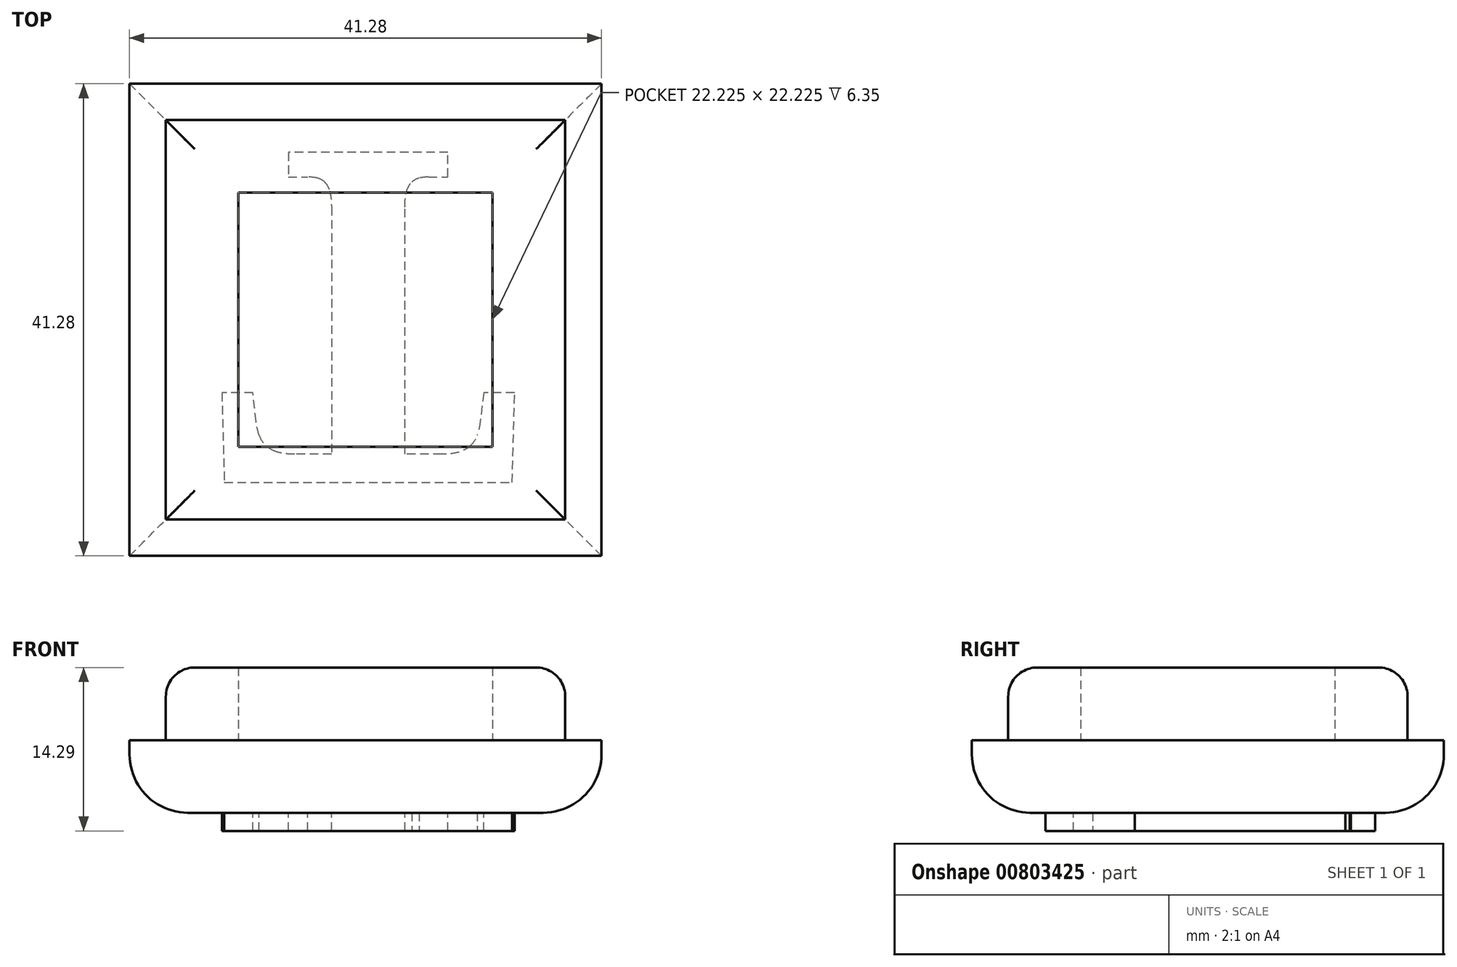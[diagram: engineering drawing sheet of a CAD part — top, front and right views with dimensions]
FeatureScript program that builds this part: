
annotation { "Feature Type Name" : "Feature", "Feature Type Description" : "" }
export const myFeature = defineFeature(function(context is Context, id is Id, definition is map)
    precondition{}
    {
        {
            var Q0;
            Q0=qCreatedBy(makeId("Top.planeOp"),FACE);
            var sketch = newSketch(context, id + "F0", { "sketchPlane" : qUnion([Q0])});
            skLineSegment(sketch, "E0.bottom", {"start": v(0, 0) * mm, "end": v(34.93, 0) * mm});
            skLineSegment(sketch, "E0.top", {"start": v(0, 34.92) * mm, "end": v(34.92, 34.92) * mm});
            skLineSegment(sketch, "E0.left", {"start": v(0, 0) * mm, "end": v(0, 34.92) * mm});
            skLineSegment(sketch, "E0.right", {"start": v(34.93, 0) * mm, "end": v(34.92, 34.92) * mm});
            skLineSegment(sketch, "E1.0", {"start": v(-3.18, -3.18) * mm, "end": v(38.1, -3.18) * mm});
            skLineSegment(sketch, "E1.1", {"start": v(-3.18, -3.18) * mm, "end": v(-3.18, 38.1) * mm});
            skLineSegment(sketch, "E1.2", {"start": v(-3.18, 38.1) * mm, "end": v(38.1, 38.1) * mm});
            skLineSegment(sketch, "E1.3", {"start": v(38.1, -3.18) * mm, "end": v(38.1, 38.1) * mm});
            skSolve(sketch);
        }
        {
            var Q0;
            Q0=makeQuery(id+"F0.imprint","IMPRINT",FACE,{"disambiguationData":[TD([[makeQuery(id+"F0.imprint","IMPRINT",EDGE,{"derivedFrom":sQuery(id+"F0.wireOp",EDGE,"E0.bottom")}),1.0]])]});
            extrude(context, id + "F1", {"entities" : qUnion([Q0]), "depth" : 12.7 * mm, "offsetDistance" : 25.4 * mm});
        }
        {
            var Q0;
            Q0=makeQuery(id+"F1.opExtrude","CAP_FACE",FACE,{"disambiguationData":[OSD([sQuery(id+"F0.wireOp",EDGE,"E0.bottom"),sQuery(id+"F0.wireOp",EDGE,"E0.top"),sQuery(id+"F0.wireOp",EDGE,"E0.left"),sQuery(id+"F0.wireOp",EDGE,"E0.right")])],"isStart":false});
            shell(context, id + "F2", {"entities" : qUnion([Q0]), "thickness" : 6.35 * mm});
        }
        {
            var Q0;
            Q0=qSketchRegion(id+"F0",true);
            extrude(context, id + "F3", {"entities" : qUnion([Q0]), "operationType" : NewBodyOperationType.ADD, "depth" : 6.35 * mm, "offsetDistance" : 25.4 * mm});
        }
        {
            var Q0;
            {var subQ0=sQuery(id+"F0.wireOp",EDGE,"E0.right");var subQ1=sQuery(id+"F0.wireOp",EDGE,"E0.left");var subQ2=sQuery(id+"F0.wireOp",EDGE,"E0.top");var subQ3=sQuery(id+"F0.wireOp",EDGE,"E0.bottom");Q0=makeQuery(id+"F3.boolean.opBoolean","MERGE",FACE,{"derivedFrom":[makeQuery(id+"F1.opExtrude","CAP_FACE",FACE,{"disambiguationData":[OSD([subQ3,subQ2,subQ1,subQ0])],"isStart":true}),makeQuery(id+"F3.opExtrude","CAP_FACE",FACE,{"disambiguationData":[OSD([subQ3,subQ2,subQ1,subQ0,sQuery(id+"F0.wireOp",EDGE,"E1.0"),sQuery(id+"F0.wireOp",EDGE,"E1.1"),sQuery(id+"F0.wireOp",EDGE,"E1.2"),sQuery(id+"F0.wireOp",EDGE,"E1.3")])],"isStart":true})]});}
            fillet(context, id + "F4", {"entities" : qUnion([Q0]), "radius" : 5.08 * mm, "tangentPropagation" : true, "allowEdgeOverflow" : false});
        }
        {
            var Q0;
            Q0=makeQuery(id+"F1.opExtrude","CAP_EDGE",EDGE,{"disambiguationData":[OSD([sQuery(id+"F0.wireOp",EDGE,"E0.top")])],"isStart":false});
            var Q1;
            Q1=makeQuery(id+"F1.opExtrude","CAP_EDGE",EDGE,{"disambiguationData":[OSD([sQuery(id+"F0.wireOp",EDGE,"E0.right")])],"isStart":false});
            var Q2;
            Q2=makeQuery(id+"F1.opExtrude","CAP_EDGE",EDGE,{"disambiguationData":[OSD([sQuery(id+"F0.wireOp",EDGE,"E0.left")])],"isStart":false});
            var Q3;
            Q3=makeQuery(id+"F1.opExtrude","CAP_EDGE",EDGE,{"disambiguationData":[OSD([sQuery(id+"F0.wireOp",EDGE,"E0.bottom")])],"isStart":false});
            fillet(context, id + "F5", {"entities" : qUnion([Q0, Q1, Q2, Q3]), "radius" : 2.54 * mm, "tangentPropagation" : true, "allowEdgeOverflow" : false});
        }
        {
            var Q0;
            {var subQ0=sQuery(id+"F0.wireOp",EDGE,"E0.right");var subQ1=sQuery(id+"F0.wireOp",EDGE,"E0.left");var subQ2=sQuery(id+"F0.wireOp",EDGE,"E0.top");var subQ3=sQuery(id+"F0.wireOp",EDGE,"E0.bottom");Q0=makeQuery(id+"F3.boolean.opBoolean","MERGE",FACE,{"derivedFrom":[makeQuery(id+"F1.opExtrude","CAP_FACE",FACE,{"disambiguationData":[OSD([subQ3,subQ2,subQ1,subQ0])],"isStart":true}),makeQuery(id+"F3.opExtrude","CAP_FACE",FACE,{"disambiguationData":[OSD([subQ3,subQ2,subQ1,subQ0,sQuery(id+"F0.wireOp",EDGE,"E1.0"),sQuery(id+"F0.wireOp",EDGE,"E1.1"),sQuery(id+"F0.wireOp",EDGE,"E1.2"),sQuery(id+"F0.wireOp",EDGE,"E1.3")])],"isStart":true})]});}
            var sketch = newSketch(context, id + "F6", { "sketchPlane" : qUnion([Q0])});
            skText(sketch, "E2", { "text": "T", "fontName": "NotoSerif-Bold.ttf"});
            const initialGuessF6  = {"E2": [0.0045, -0.0321, 1, 0, 0.0291]};
            skSetInitialGuess(sketch, initialGuessF6);
            skSolve(sketch);
        }
        {
            var Q0;
            Q0=makeQuery(id+"F6.imprint","IMPRINT",FACE,{"disambiguationData":[TD([[makeQuery(id+"F6.imprint","IMPRINT",EDGE,{"derivedFrom":sQuery(id+"F6.wireOp",EDGE,"E2.sketch_text.stroke-0")}),-1.0]])]});
            extrude(context, id + "F7", {"entities" : qUnion([Q0]), "operationType" : NewBodyOperationType.ADD, "depth" : 1.59 * mm, "offsetDistance" : 25.4 * mm});
        }
    });
